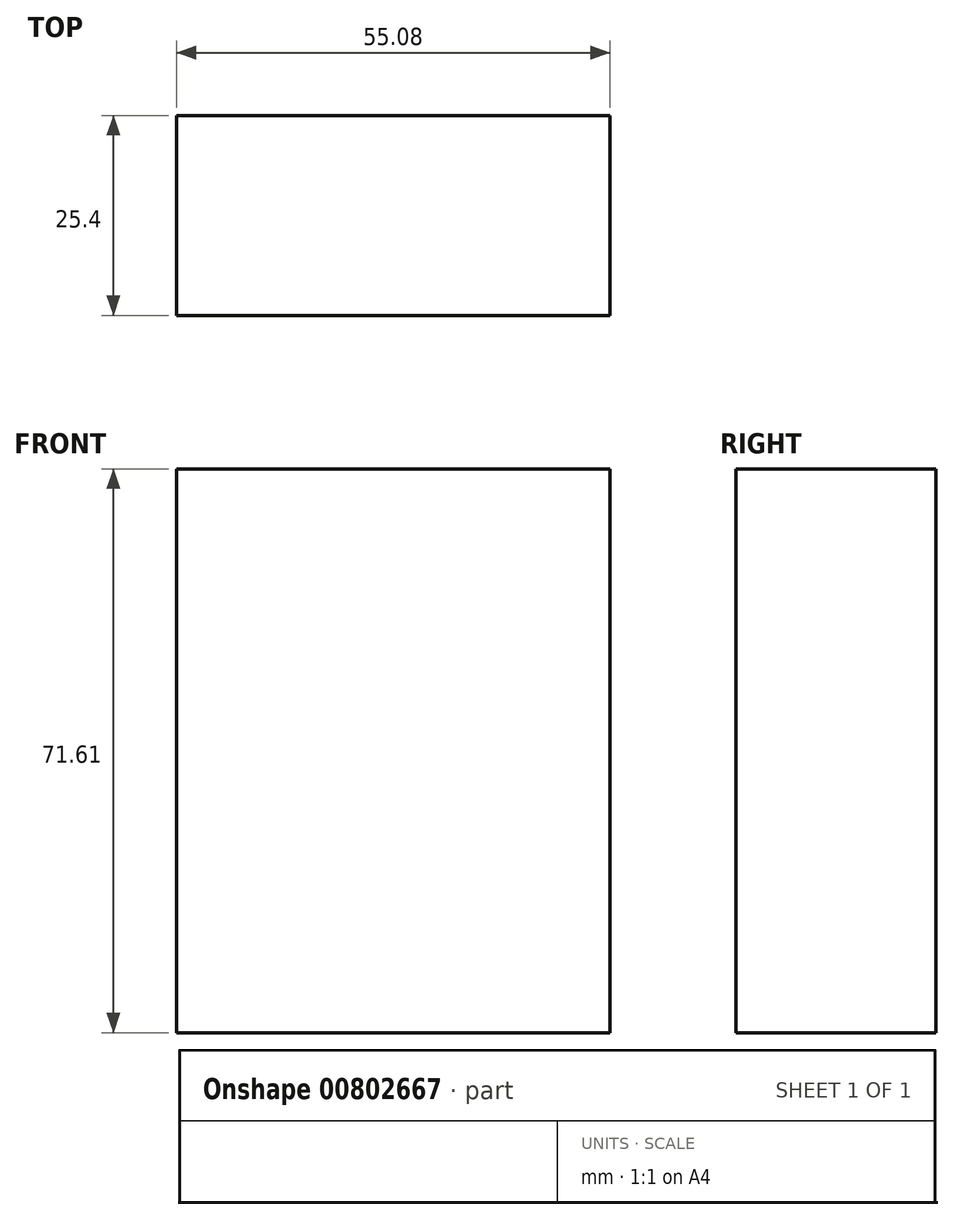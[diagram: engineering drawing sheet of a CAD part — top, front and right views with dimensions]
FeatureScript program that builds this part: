
annotation { "Feature Type Name" : "Feature", "Feature Type Description" : "" }
export const myFeature = defineFeature(function(context is Context, id is Id, definition is map)
    precondition{}
    {
        {
            var Q0;
            Q0=qCreatedBy(makeId("Front.planeOp"),FACE);
            var sketch = newSketch(context, id + "F0", { "sketchPlane" : qUnion([Q0])});
            skLineSegment(sketch, "E0.bottom", {"start": v(-142.76, 61.66) * mm, "end": v(-87.68, 61.66) * mm});
            skLineSegment(sketch, "E0.top", {"start": v(-142.76, -9.95) * mm, "end": v(-87.68, -9.95) * mm});
            skLineSegment(sketch, "E0.left", {"start": v(-142.76, 61.66) * mm, "end": v(-142.76, -9.95) * mm});
            skLineSegment(sketch, "E0.right", {"start": v(-87.68, 61.66) * mm, "end": v(-87.68, -9.95) * mm});
            skPoint(sketch, "E0.middle", {"position": v(-115.22, 25.86) * mm});
            skSolve(sketch);
        }
        {
            var Q0;
            Q0 = qSketchRegion(id + "F0", true);
            extrude(context, id + "F1", {"entities" : qUnion([Q0]), "depth" : 25.4 * mm, "offsetDistance" : 25.4 * mm});
        }
    });
